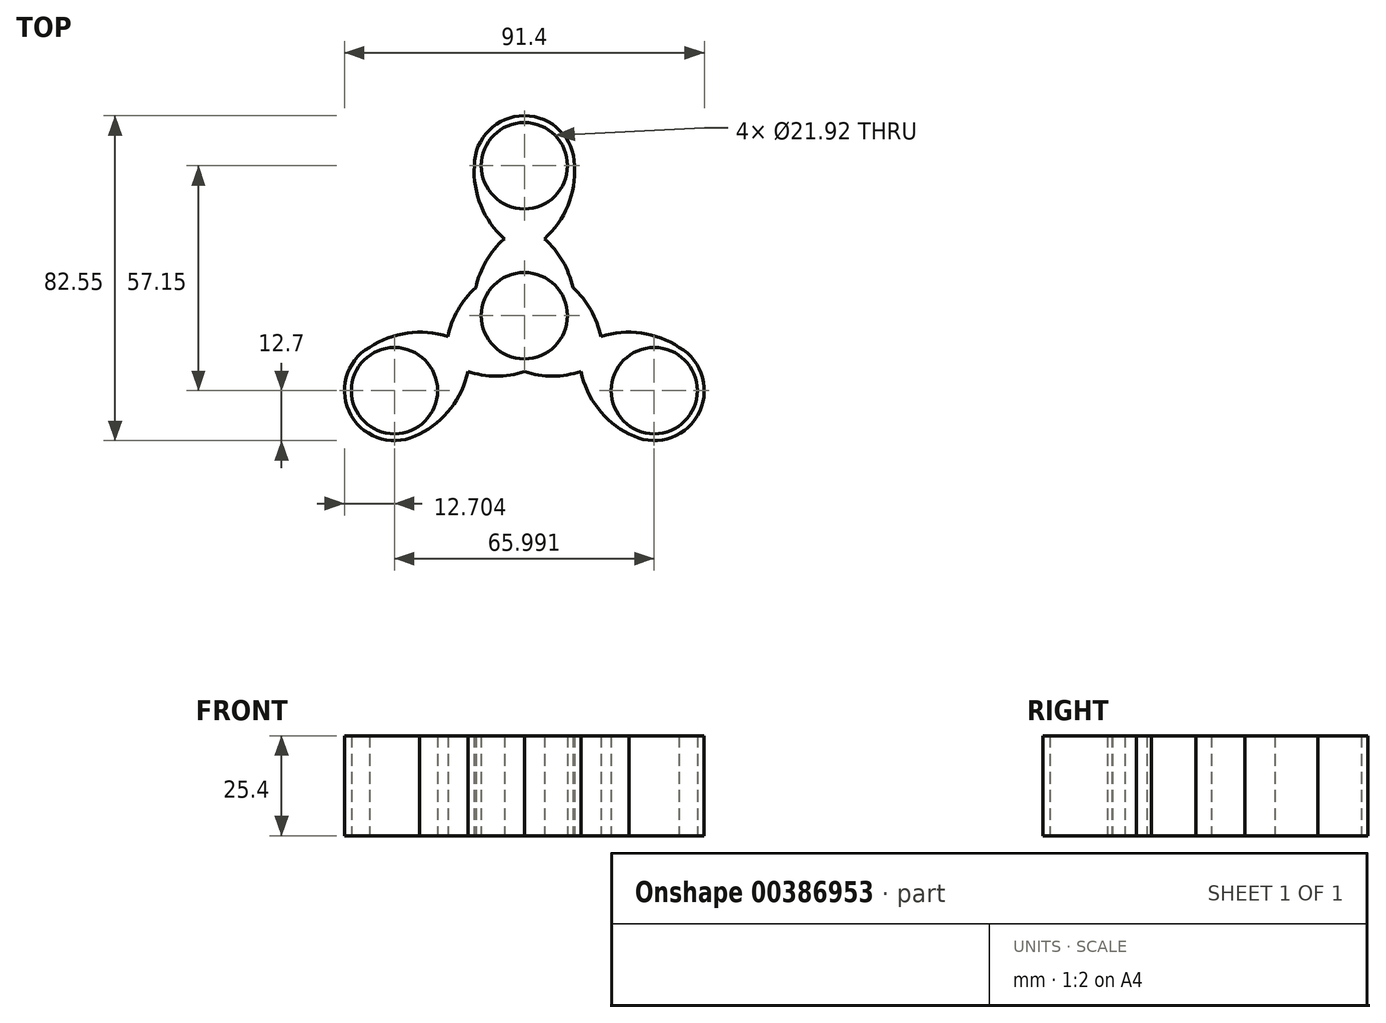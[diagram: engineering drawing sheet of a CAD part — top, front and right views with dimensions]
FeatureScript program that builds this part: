
annotation { "Feature Type Name" : "Feature", "Feature Type Description" : "" }
export const myFeature = defineFeature(function(context is Context, id is Id, definition is map)
    precondition{}
    {
        {
            var Q0;
            Q0=qCreatedBy(makeId("Top.planeOp"),FACE);
            var sketch = newSketch(context, id + "F0", { "sketchPlane" : qUnion([Q0])});
            skCircle(sketch, "E0", {"center": v(0, 0) * mm, "radius": 10.96 * mm});
            skCircle(sketch, "E1", {"center": v(0, 38.1) * mm, "radius": 10.96 * mm});
            skPoint(sketch, "E2.end.orphan", {"position": v(-10.96, 0) * mm});
            skPoint(sketch, "E3.end.orphan", {"position": v(-5.08, 19.53) * mm});
            skPoint(sketch, "E3.start.orphan", {"position": v(-10.96, 38.1) * mm});
            skPoint(sketch, "E4.end.orphan", {"position": v(10.96, 38.1) * mm});
            skPoint(sketch, "E5.end.orphan", {"position": v(5.08, 19.53) * mm});
            skPoint(sketch, "E5.start.orphan", {"position": v(10.96, 0) * mm});
            skArc(sketch, "E6", {"start": v(12.7, 38.1) * mm, "mid": v(0, 50.8) * mm, "end": v(-12.7, 38.1) * mm});
            skCircle(sketch, "E7", {"center": v(0, 0) * mm, "radius": 12.7 * mm});
            skArc(sketch, "E8", {"start": v(-12.7, 38.1) * mm, "mid": v(-11.04, 27.93) * mm, "end": v(-5.08, 19.53) * mm});
            skArc(sketch, "E9", {"start": v(5.08, 19.53) * mm, "mid": v(11.04, 27.93) * mm, "end": v(12.7, 38.1) * mm});
            skLineSegment(sketch, "E10", {"start": v(20.23, 0) * mm, "end": v(-32.1, 0) * mm, "construction": true});
            skArc(sketch, "E11", {"start": v(-5.08, 19.53) * mm, "mid": v(-9.7, 13.9) * mm, "end": v(-12.33, 7.12) * mm});
            skArc(sketch, "E12", {"start": v(12.33, 7.12) * mm, "mid": v(9.7, 13.9) * mm, "end": v(5.08, 19.53) * mm});
            skArc(sketch, "E13.1.0", {"start": v(-14.37, -14.16) * mm, "mid": v(-7.2, -15.36) * mm, "end": v(0, -14.23) * mm});
            skArc(sketch, "E13.1.1", {"start": v(-12.33, 7.12) * mm, "mid": v(-16.9, 1.45) * mm, "end": v(-19.45, -5.36) * mm});
            skArc(sketch, "E13.1.2", {"start": v(-26.65, -30.05) * mm, "mid": v(-18.67, -23.53) * mm, "end": v(-14.37, -14.16) * mm});
            skArc(sketch, "E13.1.3", {"start": v(-19.45, -5.36) * mm, "mid": v(-29.7, -4.4) * mm, "end": v(-39.35, -8.05) * mm});
            skArc(sketch, "E13.1.4", {"start": v(-39.35, -8.05) * mm, "mid": v(-44, -25.4) * mm, "end": v(-26.65, -30.05) * mm});
            skCircle(sketch, "E13.1.5", {"center": v(-33, -19.05) * mm, "radius": 10.96 * mm});
            skArc(sketch, "E13.2.0", {"start": v(19.45, -5.36) * mm, "mid": v(16.9, 1.45) * mm, "end": v(12.33, 7.12) * mm});
            skArc(sketch, "E13.2.1", {"start": v(0, -14.23) * mm, "mid": v(7.2, -15.36) * mm, "end": v(14.37, -14.16) * mm});
            skArc(sketch, "E13.2.2", {"start": v(39.35, -8.05) * mm, "mid": v(29.7, -4.4) * mm, "end": v(19.45, -5.36) * mm});
            skArc(sketch, "E13.2.3", {"start": v(14.37, -14.16) * mm, "mid": v(18.67, -23.53) * mm, "end": v(26.65, -30.05) * mm});
            skArc(sketch, "E13.2.4", {"start": v(26.65, -30.05) * mm, "mid": v(44, -25.4) * mm, "end": v(39.35, -8.05) * mm});
            skCircle(sketch, "E13.2.5", {"center": v(33, -19.05) * mm, "radius": 10.96 * mm});
            skPoint(sketch, "E14.orphan", {"position": v(6.35, -11) * mm});
            skPoint(sketch, "E15.orphan", {"position": v(-6.35, -11) * mm});
            skPoint(sketch, "E16.orphan", {"position": v(-12.7, 0) * mm});
            skPoint(sketch, "E17.orphan", {"position": v(-6.35, 11) * mm});
            skPoint(sketch, "E18.orphan", {"position": v(6.35, 11) * mm});
            skPoint(sketch, "E19.orphan", {"position": v(12.7, 0) * mm});
            skPoint(sketch, "E20.orphan", {"position": v(5.08, 39.05) * mm});
            skPoint(sketch, "E21.start.orphan", {"position": v(-5.08, 39.05) * mm});
            skPoint(sketch, "E22.orphan", {"position": v(-5.08, 0) * mm});
            skPoint(sketch, "E23.orphan", {"position": v(5.08, 0) * mm});
            skSolve(sketch);
        }
        {
            var Q0;
            Q0=makeQuery(id+"F0.imprint","IMPRINT",FACE,{"disambiguationData":[TD([[makeQuery(id+"F0.imprint","IMPRINT",EDGE,{"derivedFrom":sQuery(id+"F0.wireOp",EDGE,"E1")}),-1.0]])]});
            var Q1;
            Q1=makeQuery(id+"F0.imprint","IMPRINT",FACE,{"disambiguationData":[TD([[makeQuery(id+"F0.imprint","IMPRINT",EDGE,{"derivedFrom":sQuery(id+"F0.wireOp",EDGE,"E0")}),-1.0]])]});
            extrude(context, id + "F1", {"entities" : qUnion([Q0, Q1]), "depth" : 25.4 * mm, "offsetDistance" : 25.4 * mm});
        }
    });
